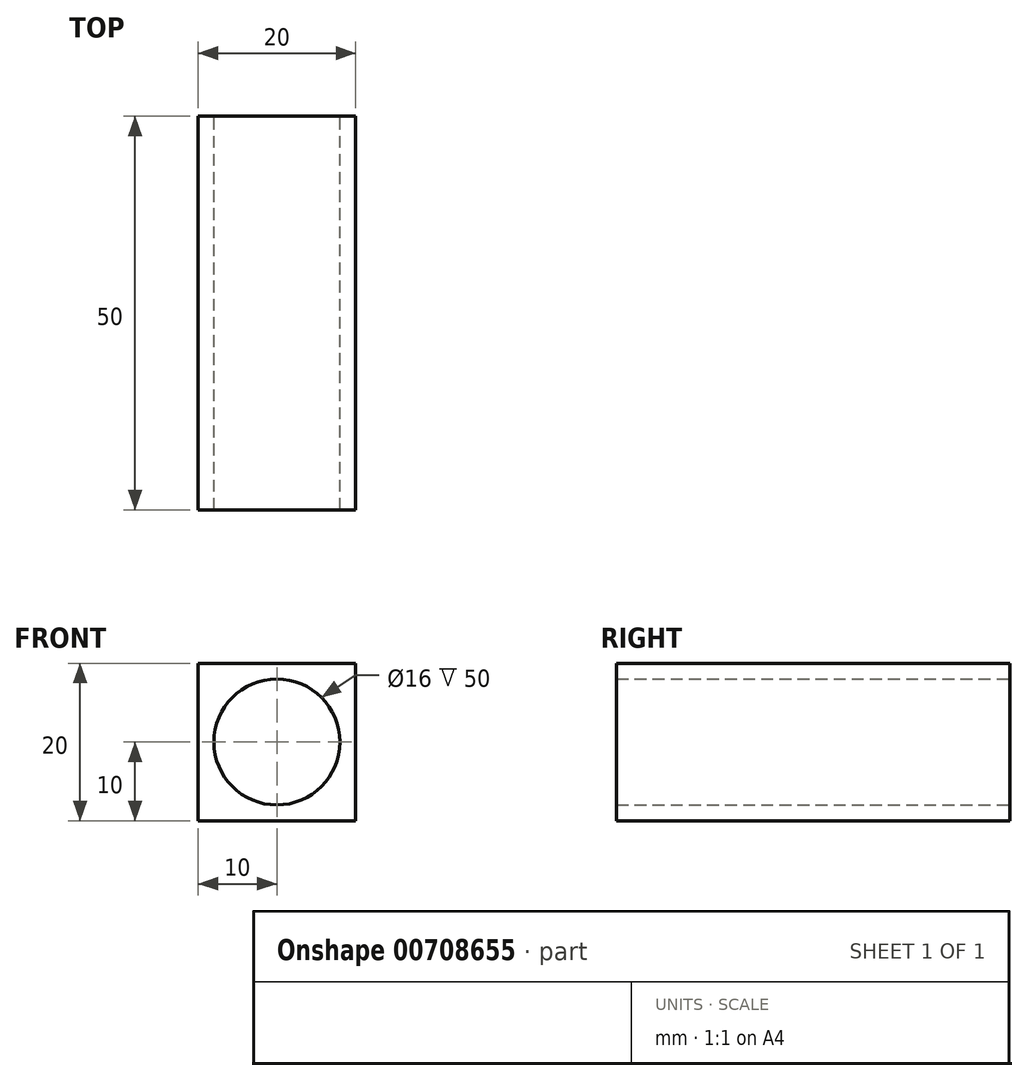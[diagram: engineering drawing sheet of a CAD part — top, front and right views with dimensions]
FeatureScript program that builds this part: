
annotation { "Feature Type Name" : "Feature", "Feature Type Description" : "" }
export const myFeature = defineFeature(function(context is Context, id is Id, definition is map)
    precondition{}
    {
        {
            var Q0;
            Q0=qCreatedBy(makeId("Front.planeOp"),FACE);
            var sketch = newSketch(context, id + "F0", { "sketchPlane" : qUnion([Q0])});
            skCircle(sketch, "E0", {"center": v(0, 0) * mm, "radius": 8 * mm});
            skLineSegment(sketch, "E1.bottom", {"start": v(-10, 10) * mm, "end": v(10, 10) * mm});
            skLineSegment(sketch, "E1.top", {"start": v(-10, -10) * mm, "end": v(10, -10) * mm});
            skLineSegment(sketch, "E1.left", {"start": v(-10, 10) * mm, "end": v(-10, -10) * mm});
            skLineSegment(sketch, "E1.right", {"start": v(10, 10) * mm, "end": v(10, -10) * mm});
            skSolve(sketch);
        }
        {
            var Q0;
            Q0=makeQuery(id+"F0.imprint","IMPRINT",FACE,{"disambiguationData":[TD([[makeQuery(id+"F0.imprint","IMPRINT",EDGE,{"derivedFrom":sQuery(id+"F0.wireOp",EDGE,"E0")}),-1.0]])]});
            extrude(context, id + "F1", {"entities" : qUnion([Q0]), "depth" : 50 * mm, "offsetDistance" : 25 * mm});
        }
    });
